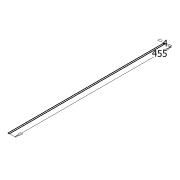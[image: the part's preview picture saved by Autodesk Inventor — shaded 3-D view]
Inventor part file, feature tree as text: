
AUTODESK INVENTOR PART (.ipt)
format: ipt  version: 2022 (Build 260153000, 153)  size: 66,048 bytes
history: native  units: mm
features: sketch x1
ambient origin geometry x8: Origin, YZ Plane, XZ Plane, XY Plane, X Axis, Y Axis, Z Axis, Center Point
feature tree (1):
  sketch  "Sketch1"  dims[d1=455.0mm d2=4.0mm]
